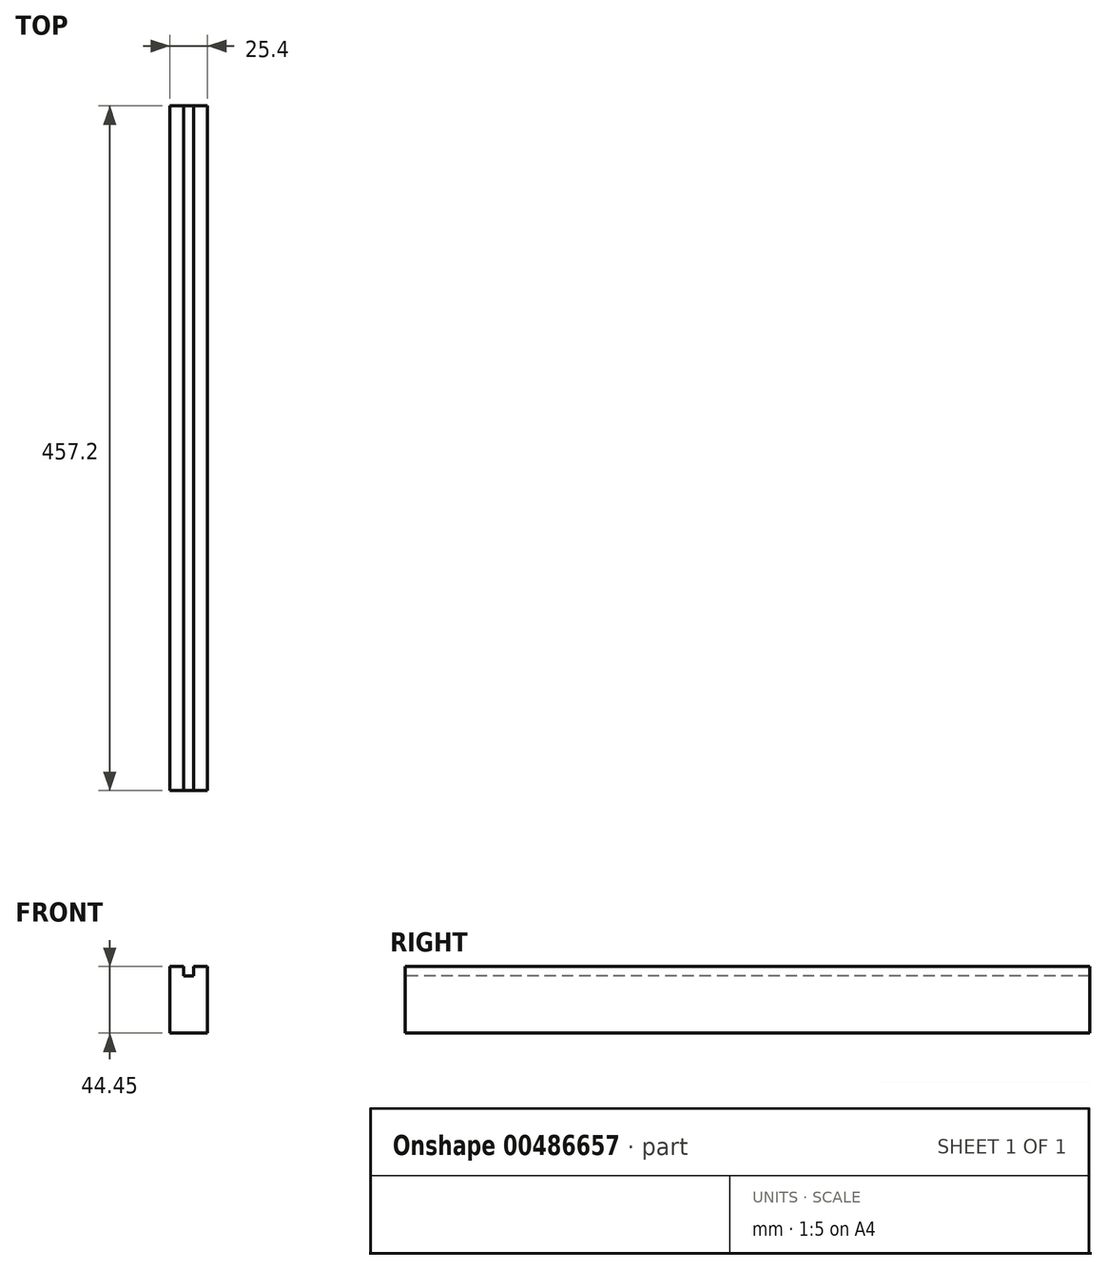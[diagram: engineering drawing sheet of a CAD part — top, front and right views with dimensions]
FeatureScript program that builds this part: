
annotation { "Feature Type Name" : "Feature", "Feature Type Description" : "" }
export const myFeature = defineFeature(function(context is Context, id is Id, definition is map)
    precondition{}
    {
        {
            var Q0;
            Q0=qCreatedBy(makeId("Top.planeOp"),FACE);
            var sketch = newSketch(context, id + "F0", { "sketchPlane" : qUnion([Q0])});
            skLineSegment(sketch, "E0.bottom", {"start": v(-12.7, 228.6) * mm, "end": v(12.7, 228.6) * mm});
            skLineSegment(sketch, "E0.top", {"start": v(-12.7, -228.6) * mm, "end": v(12.7, -228.6) * mm});
            skLineSegment(sketch, "E0.left", {"start": v(-12.7, 228.6) * mm, "end": v(-12.7, -228.6) * mm});
            skLineSegment(sketch, "E0.right", {"start": v(12.7, 228.6) * mm, "end": v(12.7, -228.6) * mm});
            skPoint(sketch, "E0.middle", {"position": v(0, 0) * mm});
            skSolve(sketch);
        }
        {
            var Q0;
            Q0 = qSketchRegion(id + "F0", true);
            extrude(context, id + "F1", {"entities" : qUnion([Q0]), "depth" : 44.45 * mm});
        }
        {
            var Q0;
            Q0=makeQuery(id+"F1.opExtrude","CAP_FACE",FACE,{"disambiguationData":[OSD([sQuery(id+"F0.wireOp",EDGE,"E0.bottom"),sQuery(id+"F0.wireOp",EDGE,"E0.top"),sQuery(id+"F0.wireOp",EDGE,"E0.left"),sQuery(id+"F0.wireOp",EDGE,"E0.right")])],"isStart":false});
            var sketch = newSketch(context, id + "F2", { "sketchPlane" : qUnion([Q0])});
            skLineSegment(sketch, "E1.bottom", {"start": v(3.18, 228.6) * mm, "end": v(-3.18, 228.6) * mm});
            skLineSegment(sketch, "E1.top", {"start": v(3.18, -228.6) * mm, "end": v(-3.18, -228.6) * mm});
            skLineSegment(sketch, "E1.left", {"start": v(3.18, 228.6) * mm, "end": v(3.18, -228.6) * mm});
            skLineSegment(sketch, "E1.right", {"start": v(-3.18, 228.6) * mm, "end": v(-3.18, -228.6) * mm});
            skPoint(sketch, "E1.middle", {"position": v(0, 0) * mm});
            skSolve(sketch);
        }
        {
            var Q0;
            Q0 = qSketchRegion(id + "F2", true);
            extrude(context, id + "F3", {"entities" : qUnion([Q0]), "operationType" : NewBodyOperationType.REMOVE, "oppositeDirection" : true, "depth" : 6.35 * mm, "offsetDistance" : 25.4 * mm});
        }
    });
